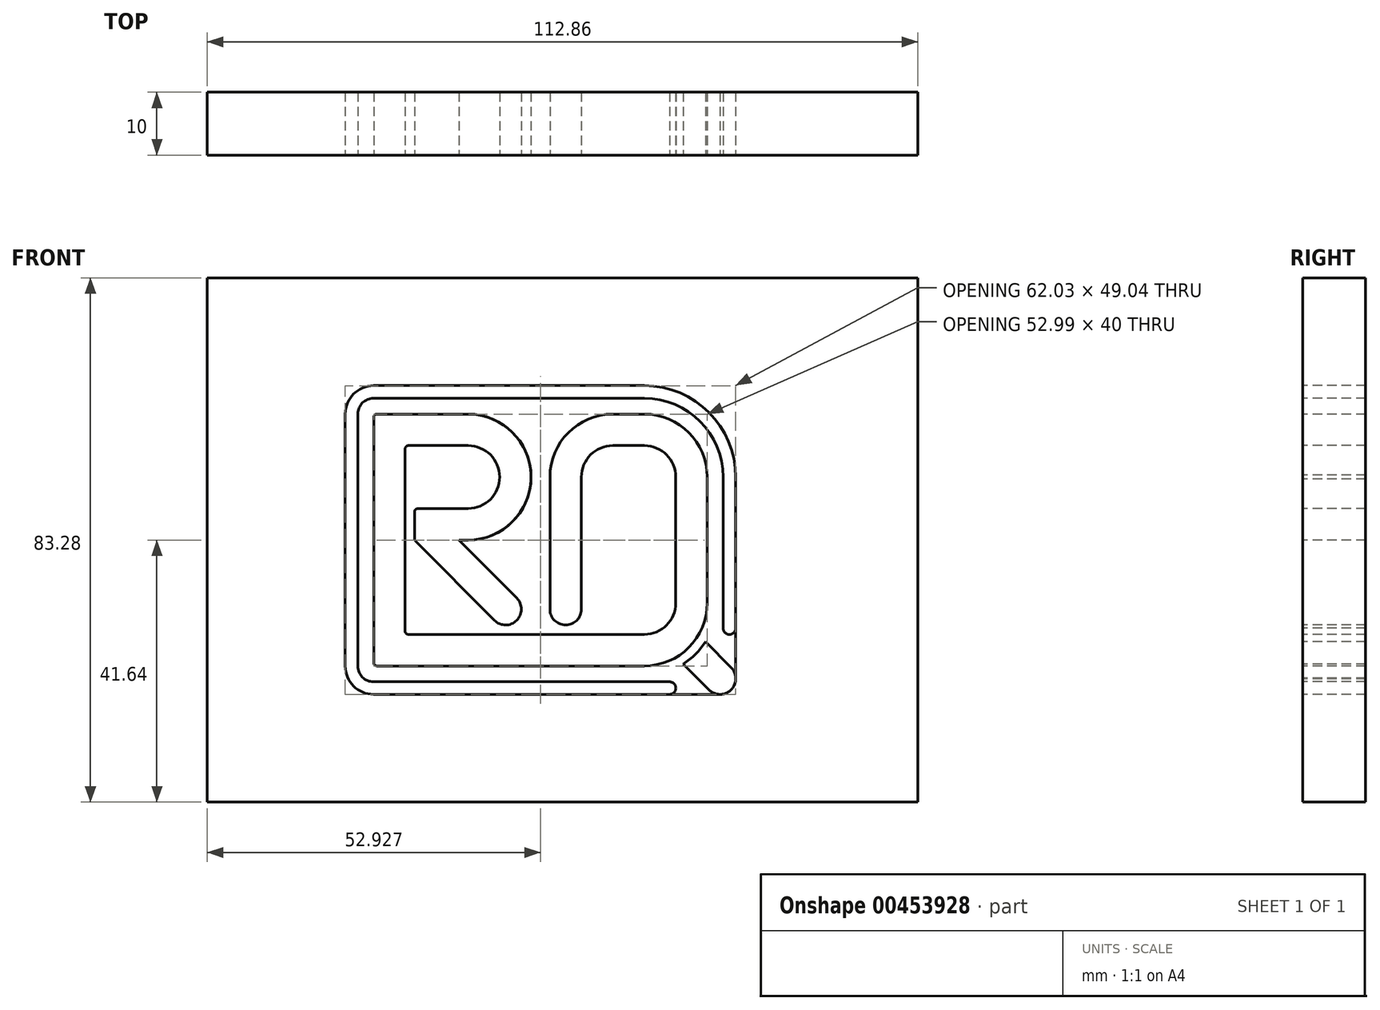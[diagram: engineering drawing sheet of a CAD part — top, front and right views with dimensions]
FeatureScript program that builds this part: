
annotation { "Feature Type Name" : "Feature", "Feature Type Description" : "" }
export const myFeature = defineFeature(function(context is Context, id is Id, definition is map)
    precondition{}
    {
        {
            var Q0;
            Q0=qCreatedBy(makeId("Front.planeOp"),FACE);
            var sketch = newSketch(context, id + "F0", { "sketchPlane" : qUnion([Q0])});
            skPoint(sketch, "E0.middle", {"position": v(0, 0) * mm});
            skLineSegment(sketch, "E1", {"start": v(-25, 14.5) * mm, "end": v(-25, -14.5) * mm});
            skLineSegment(sketch, "E2", {"start": v(-2, -20) * mm, "end": v(-0.38, -20) * mm});
            skLineSegment(sketch, "E3", {"start": v(-2, -11) * mm, "end": v(-2, 10) * mm});
            skLineSegment(sketch, "E4", {"start": v(8, 20) * mm, "end": v(13, 20) * mm});
            skLineSegment(sketch, "E5", {"start": v(23, 10) * mm, "end": v(23, -10) * mm});
            skLineSegment(sketch, "E6", {"start": v(13, -20) * mm, "end": v(9, -20) * mm});
            skLineSegment(sketch, "E7", {"start": v(-25, 20) * mm, "end": v(-15, 20) * mm});
            skLineSegment(sketch, "E8", {"start": v(-23.5, 0) * mm, "end": v(-15, 0) * mm});
            skLineSegment(sketch, "E9", {"start": v(-23.35, -0.15) * mm, "end": v(-10.82, -12.76) * mm});
            skLineSegment(sketch, "E10", {"start": v(-5, 10.33) * mm, "end": v(-5, 10.33) * mm});
            skPoint(sketch, "E11.visualSharp", {"position": v(-5.33, 20) * mm});
            skArc(sketch, "E11.filletArc", {"start": v(-5, 10.33) * mm, "mid": v(-8.05, 17.19) * mm, "end": v(-15, 20) * mm});
            skArc(sketch, "E12.filletArc", {"start": v(-15, 0) * mm, "mid": v(-7.81, 3.05) * mm, "end": v(-5, 10.33) * mm});
            skPoint(sketch, "E13.visualSharp", {"position": v(-3.63, -20) * mm});
            skPoint(sketch, "E14.visualSharp", {"position": v(23, -20) * mm});
            skArc(sketch, "E14.filletArc", {"start": v(13, -20) * mm, "mid": v(20.07, -17.07) * mm, "end": v(23, -10) * mm});
            skPoint(sketch, "E15.visualSharp", {"position": v(23, 20) * mm});
            skArc(sketch, "E15.filletArc", {"start": v(23, 10) * mm, "mid": v(20.07, 17.07) * mm, "end": v(13, 20) * mm});
            skPoint(sketch, "E16.visualSharp", {"position": v(-2, 20) * mm});
            skArc(sketch, "E16.filletArc", {"start": v(8, 20) * mm, "mid": v(0.92, 17.07) * mm, "end": v(-2, 10) * mm});
            skPoint(sketch, "E17.visualSharp", {"position": v(-2, -20) * mm});
            skArc(sketch, "E18.0", {"start": v(8, 15) * mm, "mid": v(4.46, 13.54) * mm, "end": v(3, 10) * mm});
            skLineSegment(sketch, "E18.1", {"start": v(3, -11) * mm, "end": v(3, 10) * mm});
            skLineSegment(sketch, "E18.2", {"start": v(8, 15) * mm, "end": v(13, 15) * mm});
            skArc(sketch, "E18.4", {"start": v(18, 10) * mm, "mid": v(16.53, 13.54) * mm, "end": v(13, 15) * mm});
            skLineSegment(sketch, "E18.5", {"start": v(18, 10) * mm, "end": v(18, -10) * mm});
            skArc(sketch, "E18.6", {"start": v(13, -15) * mm, "mid": v(16.53, -13.54) * mm, "end": v(18, -10) * mm});
            skLineSegment(sketch, "E18.7", {"start": v(13, -15) * mm, "end": v(9, -15) * mm});
            skLineSegment(sketch, "E19.0", {"start": v(-23, 5) * mm, "end": v(-15, 5) * mm});
            skArc(sketch, "E19.1", {"start": v(-15, 5) * mm, "mid": v(-11.44, 6.5) * mm, "end": v(-10, 10.08) * mm});
            skArc(sketch, "E19.2", {"start": v(-10, 10.08) * mm, "mid": v(-11.5, 13.56) * mm, "end": v(-15, 15) * mm});
            skLineSegment(sketch, "E19.3", {"start": v(-24.5, 15) * mm, "end": v(-15, 15) * mm});
            skLineSegment(sketch, "E20.0", {"start": v(-30, 17.5) * mm, "end": v(-30, -19.5) * mm});
            skLineSegment(sketch, "E21.0", {"start": v(-1, -15) * mm, "end": v(-0.38, -15) * mm});
            skLineSegment(sketch, "E21.2", {"start": v(-16.58, 0.12) * mm, "end": v(-7.27, -9.24) * mm});
            skLineSegment(sketch, "E22", {"start": v(-23.5, 4.5) * mm, "end": v(-23.5, 0.2) * mm});
            skLineSegment(sketch, "E23", {"start": v(-29.5, -20) * mm, "end": v(-25, -20) * mm});
            skLineSegment(sketch, "E24", {"start": v(-25, -20) * mm, "end": v(-2, -20) * mm});
            skLineSegment(sketch, "E25", {"start": v(-1, -15) * mm, "end": v(9, -15) * mm});
            skLineSegment(sketch, "E26.0", {"start": v(-24.5, -15) * mm, "end": v(0, -15) * mm});
            skLineSegment(sketch, "E27", {"start": v(-5, 10.33) * mm, "end": v(-5, 0) * mm});
            skLineSegment(sketch, "E28", {"start": v(0.5, -13.5) * mm, "end": v(0.5, -13.5) * mm});
            skPoint(sketch, "E29.visualSharp", {"position": v(3, -13.5) * mm});
            skArc(sketch, "E29.filletArc", {"start": v(0.5, -13.5) * mm, "mid": v(2.26, -12.77) * mm, "end": v(3, -11) * mm});
            skPoint(sketch, "E30.newPointB", {"position": v(-23.5, -13.5) * mm});
            skArc(sketch, "E30.filletArc", {"start": v(-2, -11) * mm, "mid": v(-1.27, -12.77) * mm, "end": v(0.5, -13.5) * mm});
            skPoint(sketch, "E31.visualSharp", {"position": v(-30, -20) * mm});
            skArc(sketch, "E31.filletArc", {"start": v(-30, -19.5) * mm, "mid": v(-29.85, -19.85) * mm, "end": v(-29.5, -20) * mm});
            skLineSegment(sketch, "E32", {"start": v(-7.28, -12.77) * mm, "end": v(-7.28, -12.77) * mm});
            skArc(sketch, "E33.filletArc", {"start": v(-7.28, -12.77) * mm, "mid": v(-6.55, -11) * mm, "end": v(-7.27, -9.24) * mm});
            skArc(sketch, "E34.filletArc", {"start": v(-10.82, -12.76) * mm, "mid": v(-9.05, -13.5) * mm, "end": v(-7.28, -12.77) * mm});
            skLineSegment(sketch, "E35.0", {"start": v(19.16, -19.7) * mm, "end": v(23.25, -23.79) * mm});
            skLineSegment(sketch, "E36.0", {"start": v(22.7, -16.17) * mm, "end": v(26.78, -20.25) * mm});
            skLineSegment(sketch, "E37.0", {"start": v(14.76, -15.3) * mm, "end": v(14.29, -14.83) * mm});
            skPoint(sketch, "E38.newPointB", {"position": v(-25, 20) * mm});
            skArc(sketch, "E38.filletArc", {"start": v(-24.5, 15) * mm, "mid": v(-24.85, 14.85) * mm, "end": v(-25, 14.5) * mm});
            skPoint(sketch, "E39.visualSharp", {"position": v(-23.5, 5) * mm});
            skArc(sketch, "E39.filletArc", {"start": v(-23, 5) * mm, "mid": v(-23.35, 4.85) * mm, "end": v(-23.5, 4.5) * mm});
            skPoint(sketch, "E40.visualSharp", {"position": v(-23.5, 0) * mm});
            skArc(sketch, "E40.filletArc", {"start": v(-23.5, 0.2) * mm, "mid": v(-23.46, 0.02) * mm, "end": v(-23.35, -0.15) * mm});
            skLineSegment(sketch, "E41", {"start": v(-30, 17.5) * mm, "end": v(-30, 19.5) * mm});
            skLineSegment(sketch, "E42", {"start": v(-25, 20) * mm, "end": v(-29.5, 20) * mm});
            skPoint(sketch, "E43.visualSharp", {"position": v(-30, 20) * mm});
            skArc(sketch, "E43.filletArc", {"start": v(-29.5, 20) * mm, "mid": v(-29.85, 19.85) * mm, "end": v(-30, 19.5) * mm});
            skArc(sketch, "E44", {"start": v(23.25, -23.79) * mm, "mid": v(26.78, -23.79) * mm, "end": v(26.78, -20.25) * mm});
            skPoint(sketch, "E45", {"position": v(20.07, -17.07) * mm});
            skPoint(sketch, "E46.orphan", {"position": v(16.53, -13.54) * mm});
            skLineSegment(sketch, "E47.trimOffspring", {"start": v(13, -20) * mm, "end": v(-0.38, -20) * mm});
            skArc(sketch, "E48.trimOffspring", {"start": v(19.16, -19.7) * mm, "mid": v(21.13, -18.13) * mm, "end": v(22.7, -16.17) * mm});
            skPoint(sketch, "E49.newPointB", {"position": v(-25, -20) * mm});
            skArc(sketch, "E49.filletArc", {"start": v(-25, -14.5) * mm, "mid": v(-24.85, -14.85) * mm, "end": v(-24.5, -15) * mm});
            skLineSegment(sketch, "E50", {"start": v(-15, 20) * mm, "end": v(8, 20) * mm});
            skLineSegment(sketch, "E51", {"start": v(21.86, -24.52) * mm, "end": v(-30.02, -24.52) * mm});
            skLineSegment(sketch, "E52", {"start": v(27.51, -22.08) * mm, "end": v(27.51, -18.86) * mm});
            skLineSegment(sketch, "E53", {"start": v(13, 24.52) * mm, "end": v(-30.02, 24.52) * mm});
            skLineSegment(sketch, "E54", {"start": v(-34.52, -20.02) * mm, "end": v(-34.52, 20.02) * mm});
            skPoint(sketch, "E55.orphan", {"position": v(17.43, -17.97) * mm});
            skPoint(sketch, "E56.orphan", {"position": v(13.35, -13.89) * mm});
            skArc(sketch, "E57.0", {"start": v(27.51, 10) * mm, "mid": v(23.26, 20.27) * mm, "end": v(13, 24.52) * mm});
            skArc(sketch, "E58.0", {"start": v(25.51, 10) * mm, "mid": v(21.85, 18.85) * mm, "end": v(13, 22.52) * mm});
            skLineSegment(sketch, "E59.0", {"start": v(25.51, -22.07) * mm, "end": v(25.51, -18.98) * mm});
            skLineSegment(sketch, "E60.0", {"start": v(25.02, -22.52) * mm, "end": v(21.98, -22.52) * mm});
            skLineSegment(sketch, "E61.0", {"start": v(-32.52, -20.02) * mm, "end": v(-32.52, 20.02) * mm});
            skLineSegment(sketch, "E62.0", {"start": v(13, 22.52) * mm, "end": v(-30.02, 22.52) * mm});
            skPoint(sketch, "E63.visualSharp", {"position": v(-32.52, 22.52) * mm});
            skArc(sketch, "E63.filletArc", {"start": v(-30.02, 22.52) * mm, "mid": v(-31.79, 21.79) * mm, "end": v(-32.52, 20.02) * mm});
            skArc(sketch, "E64.0", {"start": v(-30.02, 24.52) * mm, "mid": v(-33.2, 23.2) * mm, "end": v(-34.52, 20.02) * mm});
            skPoint(sketch, "E65.visualSharp", {"position": v(-32.52, -22.52) * mm});
            skArc(sketch, "E65.filletArc", {"start": v(-32.52, -20.02) * mm, "mid": v(-31.79, -21.79) * mm, "end": v(-30.02, -22.52) * mm});
            skArc(sketch, "E66.0", {"start": v(-34.52, -20.02) * mm, "mid": v(-33.2, -23.2) * mm, "end": v(-30.02, -24.52) * mm});
            skLineSegment(sketch, "E67", {"start": v(26.51, -15) * mm, "end": v(26.51, -16.32) * mm});
            skLineSegment(sketch, "E68.0", {"start": v(18.1, -20.77) * mm, "end": v(22.19, -24.85) * mm, "construction": true});
            skLineSegment(sketch, "E69.0", {"start": v(23.76, -15.1) * mm, "end": v(27.84, -19.2) * mm, "construction": true});
            skArc(sketch, "E70", {"start": v(17, -24.52) * mm, "mid": v(18, -23.52) * mm, "end": v(17, -22.52) * mm});
            skCircle(sketch, "E71", {"center": v(26.51, -14) * mm, "radius": 1 * mm});
            skLineSegment(sketch, "E72.trimOffspring", {"start": v(25.51, -14) * mm, "end": v(25.51, 10) * mm});
            skLineSegment(sketch, "E73.trimOffspring", {"start": v(27.51, -14) * mm, "end": v(27.51, 33) * mm});
            skLineSegment(sketch, "E74.trimOffspring", {"start": v(19.86, -22.52) * mm, "end": v(-30.02, -22.52) * mm});
            skLineSegment(sketch, "E75", {"start": v(21.86, -24.52) * mm, "end": v(25.02, -24.52) * mm});
            skLineSegment(sketch, "E76", {"start": v(27.51, -14) * mm, "end": v(27.51, -22.08) * mm});
            skLineSegment(sketch, "E77.bottom", {"start": v(-56.43, 41.64) * mm, "end": v(56.43, 41.64) * mm});
            skLineSegment(sketch, "E77.top", {"start": v(-56.43, -41.64) * mm, "end": v(56.43, -41.64) * mm});
            skLineSegment(sketch, "E77.left", {"start": v(-56.43, 41.64) * mm, "end": v(-56.43, -41.64) * mm});
            skLineSegment(sketch, "E77.right", {"start": v(56.43, 41.64) * mm, "end": v(56.43, -41.64) * mm});
            skLineSegment(sketch, "E78", {"start": v(0, 0) * mm, "end": v(0, -38.7) * mm, "construction": true});
            skLineSegment(sketch, "E79", {"start": v(0, 0) * mm, "end": v(33.56, 0) * mm, "construction": true});
            skSolve(sketch);
        }
        {
            var Q0;
            Q0=makeQuery(id+"F0.imprint","IMPRINT",FACE,{"disambiguationData":[TD([[makeQuery(id+"F0.imprint","IMPRINT",EDGE,{"derivedFrom":sQuery(id+"F0.wireOp",EDGE,"E1")}),-1.0]])]});
            var Q1;
            {var subQ6=sQuery(id+"F0.wireOp",EDGE,"E9");Q1=makeQuery(id+"F0.imprint","IMPRINT",FACE,{"disambiguationData":[TD([[makeQuery(id+"F0.imprint","IMPRINT",EDGE,{"derivedFrom":subQ6}),1.0]])]});}
            var Q2;
            {var subQ0=sQuery(id+"F0.wireOp",EDGE,"E44");var subQ1=makeQuery(id+"F0.imprint","INTERSECT",VERTEX,{"derivedFrom":[sQuery(id+"F0.wireOp",EDGE,"E36.0"),subQ0]});Q2=makeQuery(id+"F0.imprint","IMPRINT",FACE,{"disambiguationData":[TD([[makeQuery(id+"F0.imprint","IMPRINT",EDGE,{"disambiguationData":[TD([[subQ1,-1.0]])],"derivedFrom":subQ0}),1.0]])]});}
            var Q3;
            {var subQ1=sQuery(id+"F0.wireOp",EDGE,"E36.0");Q3=makeQuery(id+"F0.imprint","IMPRINT",FACE,{"disambiguationData":[TD([[makeQuery(id+"F0.imprint","IMPRINT",EDGE,{"derivedFrom":subQ1}),-1.0]])]});}
            var Q4;
            {var subQ0=sQuery(id+"F0.wireOp",EDGE,"E0.bottom");Q4=makeQuery(id+"F0.imprint","IMPRINT",FACE,{"disambiguationData":[TD([[makeQuery(id+"F0.imprint","IMPRINT",EDGE,{"derivedFrom":subQ0}),-1.0]])]});}
            var Q5;
            {var subQ0=sQuery(id+"F0.wireOp",EDGE,"E0.bottom");Q5=makeQuery(id+"F0.imprint","IMPRINT",FACE,{"disambiguationData":[TD([[makeQuery(id+"F0.imprint","IMPRINT",EDGE,{"derivedFrom":subQ0}),1.0]])]});}
            extrude(context, id + "F1", {"entities" : qUnion([Q0, Q1, Q2, Q3, Q4, Q5]), "oppositeDirection" : true, "depth" : 10 * mm});
        }
        {
            var Q0;
            Q0=makeQuery(id+"F0.imprint","IMPRINT",FACE,{"disambiguationData":[TD([[makeQuery(id+"F0.imprint","IMPRINT",EDGE,{"derivedFrom":sQuery(id+"F0.wireOp",EDGE,"E1")}),1.0]])]});
            var Q1;
            {var subQ16=sQuery(id+"F0.wireOp",EDGE,"E2");Q1=makeQuery(id+"F0.imprint","IMPRINT",FACE,{"disambiguationData":[TD([[makeQuery(id+"F0.imprint","IMPRINT",EDGE,{"derivedFrom":subQ16}),-1.0]])]});}
            extrude(context, id + "F2", {"entities" : qUnion([Q0, Q1]), "oppositeDirection" : true, "depth" : 10 * mm});
        }
        {
            var Q0;
            Q0=makeQuery(id+"F0.imprint","IMPRINT",FACE,{"disambiguationData":[TD([[makeQuery(id+"F0.imprint","IMPRINT",EDGE,{"derivedFrom":sQuery(id+"F0.wireOp",EDGE,"E53")}),1.0]])]});
            var Q1;
            {var subQ0=sQuery(id+"F0.wireOp",EDGE,"E70");var subQ2=makeQuery(id+"F0.imprint","IMPRINT",VERTEX,{"derivedFrom":subQ0});Q1=makeQuery(id+"F0.imprint","IMPRINT",FACE,{"disambiguationData":[TD([[makeQuery(id+"F0.imprint","IMPRINT",EDGE,{"disambiguationData":[TD([[subQ2,-1.0]])],"derivedFrom":subQ0}),1.0]])]});}
            var Q2;
            {var subQ0=sQuery(id+"F0.wireOp",EDGE,"E71");var subQ3=makeQuery(id+"F0.imprint","IMPRINT",VERTEX,{"derivedFrom":subQ0});Q2=makeQuery(id+"F0.imprint","IMPRINT",FACE,{"disambiguationData":[TD([[makeQuery(id+"F0.imprint","IMPRINT",EDGE,{"disambiguationData":[TD([[subQ3,1.0]])],"derivedFrom":subQ0}),1.0]])]});}
            extrude(context, id + "F3", {"entities" : qUnion([Q0, Q1, Q2]), "oppositeDirection" : true, "depth" : 10 * mm});
        }
        {
            var Q0;
            Q0=makeQuery(id+"F0.imprint","IMPRINT",FACE,{"disambiguationData":[TD([[makeQuery(id+"F0.imprint","IMPRINT",EDGE,{"derivedFrom":sQuery(id+"F0.wireOp",EDGE,"E53")}),-1.0]])]});
            extrude(context, id + "F4", {"entities" : qUnion([Q0]), "oppositeDirection" : true, "depth" : 10 * mm});
        }
    });
